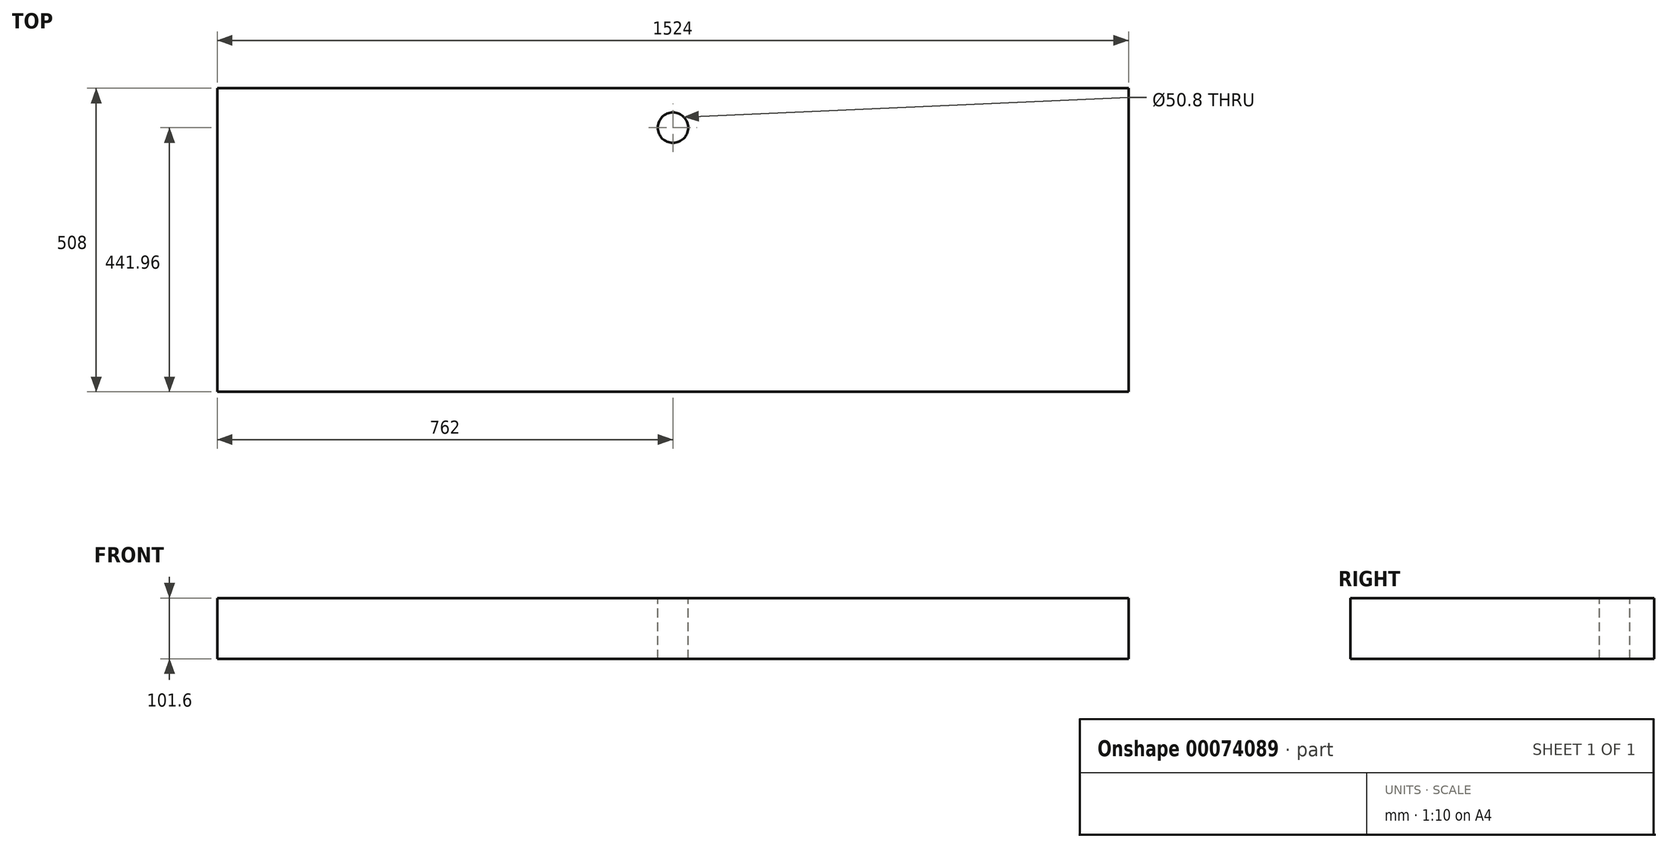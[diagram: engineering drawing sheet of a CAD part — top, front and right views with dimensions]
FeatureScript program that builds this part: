
annotation { "Feature Type Name" : "Feature", "Feature Type Description" : "" }
export const myFeature = defineFeature(function(context is Context, id is Id, definition is map)
    precondition{}
    {
        {
            var Q0;
            Q0=qCreatedBy(makeId("Top.planeOp"),FACE);
            var sketch = newSketch(context, id + "F0", { "sketchPlane" : qUnion([Q0])});
            skLineSegment(sketch, "E0.rect.bottom", {"start": v(762, -254) * mm, "end": v(-762, -254) * mm});
            skLineSegment(sketch, "E0.rect.top", {"start": v(762, 254) * mm, "end": v(-762, 254) * mm});
            skLineSegment(sketch, "E0.rect.left", {"start": v(762, -254) * mm, "end": v(762, 254) * mm});
            skLineSegment(sketch, "E0.rect.right", {"start": v(-762, -254) * mm, "end": v(-762, 254) * mm});
            skPoint(sketch, "E0.rect.middle", {"position": v(0, 0) * mm});
            skSolve(sketch);
        }
        {
            var Q0;
            Q0=makeQuery(id+"F0.imprint","IMPRINT",FACE,{"disambiguationData":[TD([[makeQuery(id+"F0.imprint","IMPRINT",EDGE,{"derivedFrom":sQuery(id+"F0.wireOp",EDGE,"E0.rect.bottom")}),-1.0]])]});
            extrude(context, id + "F1", {"entities" : qUnion([Q0]), "endBound" : BoundingType.SYMMETRIC, "depth" : 101.6 * mm});
        }
        {
            var Q0;
            Q0=makeQuery(id+"F1.opExtrude","CAP_FACE",FACE,{"disambiguationData":[OSD([sQuery(id+"F0.wireOp",EDGE,"E0.rect.bottom"),sQuery(id+"F0.wireOp",EDGE,"E0.rect.top"),sQuery(id+"F0.wireOp",EDGE,"E0.rect.left"),sQuery(id+"F0.wireOp",EDGE,"E0.rect.right")])],"isStart":false});
            var sketch = newSketch(context, id + "F2", { "sketchPlane" : qUnion([Q0])});
            skCircle(sketch, "E1", {"center": v(0, 187.96) * mm, "radius": 25.4 * mm});
            skSolve(sketch);
        }
        {
            var Q0;
            Q0=makeQuery(id+"F2.imprint","IMPRINT",FACE,{"disambiguationData":[TD([[makeQuery(id+"F2.imprint","IMPRINT",EDGE,{"derivedFrom":sQuery(id+"F2.wireOp",EDGE,"E1")}),1.0]])]});
            extrude(context, id + "F3", {"entities" : qUnion([Q0]), "operationType" : NewBodyOperationType.REMOVE, "oppositeDirection" : true, "depth" : 130.34 * mm});
        }
    });
